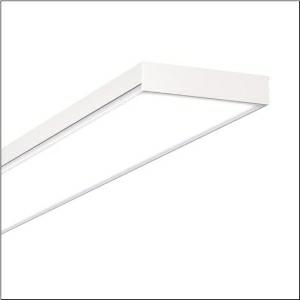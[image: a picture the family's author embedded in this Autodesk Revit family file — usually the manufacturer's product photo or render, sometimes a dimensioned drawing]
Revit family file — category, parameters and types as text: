
# Revit family: apollon_r__31_51mp25wm2441w_0650
name_source: partatom
category: Lighting Fixtures
units: mm (PartAtom-declared; Revit-internal decimal feet)

## family parameters
Cut with Voids When Loaded = No
Host = Face
Light Source = No
Part Type = Normal
Room Calculation Point = No
Round Connector Dimension = Use Diameter
Shared = No

## types (1)
- Apollon® 31 (1 x LED, 3800 lm, 27 W, 4000K)
    Apparent Load = 27 VA
    CIE Flux Codes = 61 87 97 97 100
    Color Rendering = 80
    Color Temperature = 4000K
    Default Elevation = 1800 mm
    Description = Apollon® 31, office luminaire, primary optical cover: micro prismatic cover, of PMMA, light emission: direct distribution, primary light characteristic: symmetric, installation type: surface-mounted, LED, rated luminous flux: 3.800lm, luminous efficacy: 139lm/W, light colour: 840, colour temperature: 4000K, control gear: ECG Multilumen, with terminal, 3-pole, mains connection: 220..240V, AC, 50/60Hz, rated input power: 27W, housing, of sheet steel, coil coated, traffic white (RAL 9016), length: 1.245mm, width: 200mm, height: 44mm, protection rating (complete): IP20, insulation class (complete): insulation class II (safety insulation), certification: CE, impact resistance: IK02, permissible operating ambient temperature: -20..+40°C, packaging unit: 1 piece
    Height = 44 mm
    Lamp = 1 x LED
    Lamp Light Flux = 3800 lm
    Lamp Power = 27 W
    Lamp count = 1
    Length = 1245 mm
    Luminous efficacy = 141 lm/W
    Manufacturer = Siteco
    ModVariant = No
    Model = 51MP25WM2441W
    Mounting Place = Ceiling
    Mounting Type = Surface mounted
    Number of Poles = 1
    OnlyDefault = Yes
    Power Factor = 1
    Product Name = Apollon® 31
    Product group = office luminaire | ceiling mounted
    ProductGroupID = 302
    Protection Class = Protection class II
    Protection Degree = IP 20
    RLX_Detail_Level = 1
    RlxData = <blob elided: 20729 chars, md5=34ea9248>
    Socket = socket
    Standby Power = 0 W
    System Light Flux = 3800 lm
    System Power = 27 W
    Type Comments = Product without accessories
    Type Image = l_1007095.jpg
    URL = http://relux.com
    VarID = ---
    Voltage = 0 V
    Weight = 0.00 kg
    Width = 200 mm  [stored 0.656168 ft]

note: [stored X ft] marks values corroborated as IEEE doubles in the binary element streams (Revit-internal decimal feet)

## geometry (parser evidence)
native form markers: Blend x4, Sweep x9
no freeform markers — native parametric forms only
